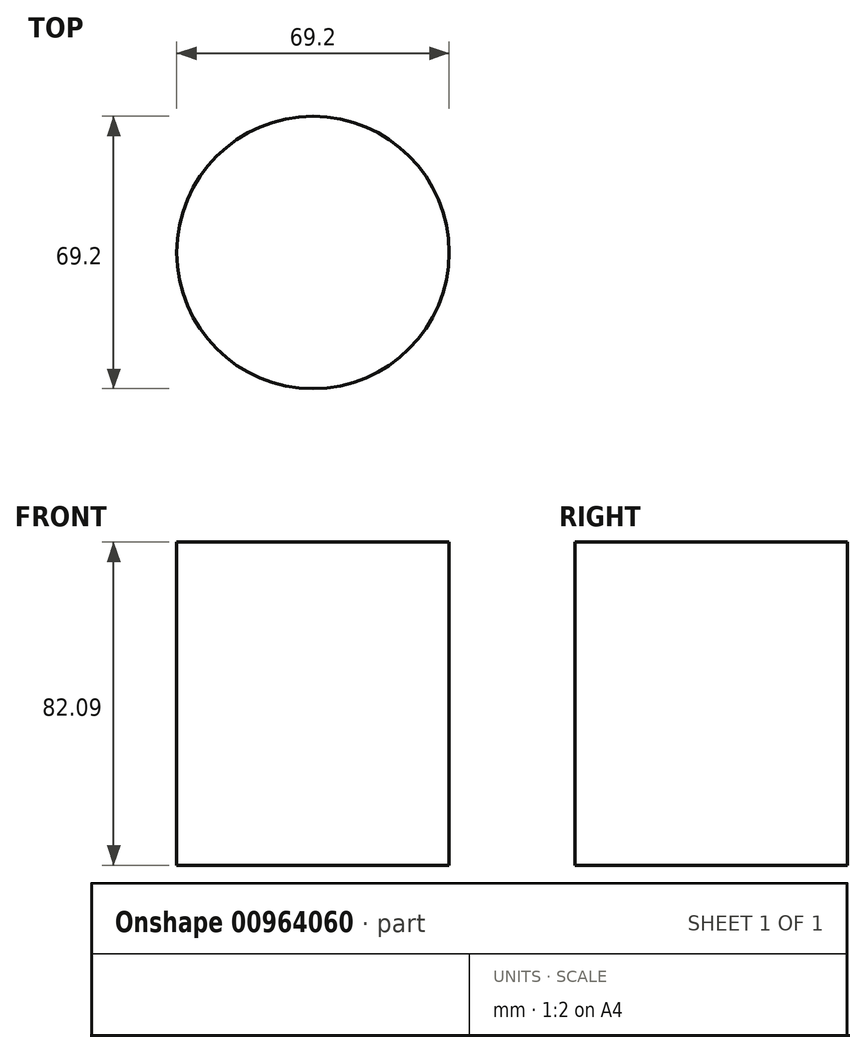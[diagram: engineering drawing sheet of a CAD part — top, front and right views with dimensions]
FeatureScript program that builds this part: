
annotation { "Feature Type Name" : "Feature", "Feature Type Description" : "" }
export const myFeature = defineFeature(function(context is Context, id is Id, definition is map)
    precondition{}
    {
        {
            var Q0;
            Q0=qCreatedBy(makeId("Front.planeOp"),FACE);
            var sketch = newSketch(context, id + "F0", { "sketchPlane" : qUnion([Q0])});
            skLineSegment(sketch, "E0", {"start": v(0, 45.02) * mm, "end": v(-34.6, 45.02) * mm});
            skLineSegment(sketch, "E1", {"start": v(-34.6, 45.02) * mm, "end": v(-34.6, -37.07) * mm});
            skLineSegment(sketch, "E2", {"start": v(-34.6, -37.07) * mm, "end": v(0, -37.07) * mm});
            skLineSegment(sketch, "E3", {"start": v(0, -37.07) * mm, "end": v(0, 45.02) * mm});
            skSolve(sketch);
        }
        {
            var Q0;
            Q0 = qSketchRegion(id + "F0", true);
            var Q1;
            Q1=sQuery(id+"F0.wireOp",EDGE,"E3");
            revolve(context, id + "F1", {"surfaceOperationType" : NewSurfaceOperationType.NEW, "entities" : qUnion([Q0]), "axis" : qUnion([Q1]), "revolveType" : RevolveType.FULL});
        }
    });
